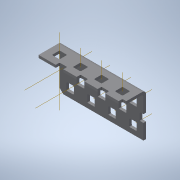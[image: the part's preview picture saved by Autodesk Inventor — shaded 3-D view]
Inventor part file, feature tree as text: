
AUTODESK INVENTOR PART (.ipt)
format: ipt  version: 2020 (Build 240168000, 168)  size: 1,925,632 bytes
history: native  units: in
note: dims shown in document units (in); Inventor stores cm internally (conversion verified against a paired STEP export)
features: other x21, pattern_linear x3, sheet_metal_op x1, extrude x1, plane x1, split x1, imported_body x1, sketch x1
ambient origin geometry x8: Origin, YZ Plane, XZ Plane, XY Plane, X Axis, Y Axis, Z Axis, Center Point
bodies: Body1 (feature_tree)
feature tree (30):
  sheet_metal_op  "Fold1"
  other  "L-Channel"
  extrude  "length cut"  Depth=0.5in
  other  "top out axis"
  other  "back out axis"
  other  "back inner axis"
  pattern_linear  "top outer axes"  Spacing1=0.3937in  [1 undecoded]
  pattern_linear  "back outer axes"  Count1=2 Spacing1=0.5in
  pattern_linear  "back inner axes"  Spacing1=0.5in  [1 undecoded]
  other  "right plane"
  plane  "Work Plane3"
  split  "Split1"
  imported_body  "Base1"
  sketch  "Sketch1"  dims[d1=0.0in d4=0.5in d5=0.3937in d7=0.5in d13=0.5in d14=0.7874in d16=0.5in d19=0.5in d20=-2.0in d21=0.0in d22=0.0in d23=0.0in d24=0.0in d25=0.0in d26=0.0in]
  other  "Work Point1"
  other  "Work Point3"
  other  "Work Point4"
  other  "Work Axis5"
  other  "Work Axis6"
  other  "Work Axis7"
  other  "Work Axis23"
  other  "Work Axis24"
  other  "Work Axis25"
  other  "Work Axis29"
  other  "Work Axis30"
  other  "Work Axis31"
  other  "Work Axis32"
  other  "Work Axis36"
  other  "Work Axis37"
  other  "left plane"
note: 2 required parameter values undecoded (feature->parameter linkage not recoverable at this tier; creation-order binding heuristic only, values carry confidence <= 0.55)
